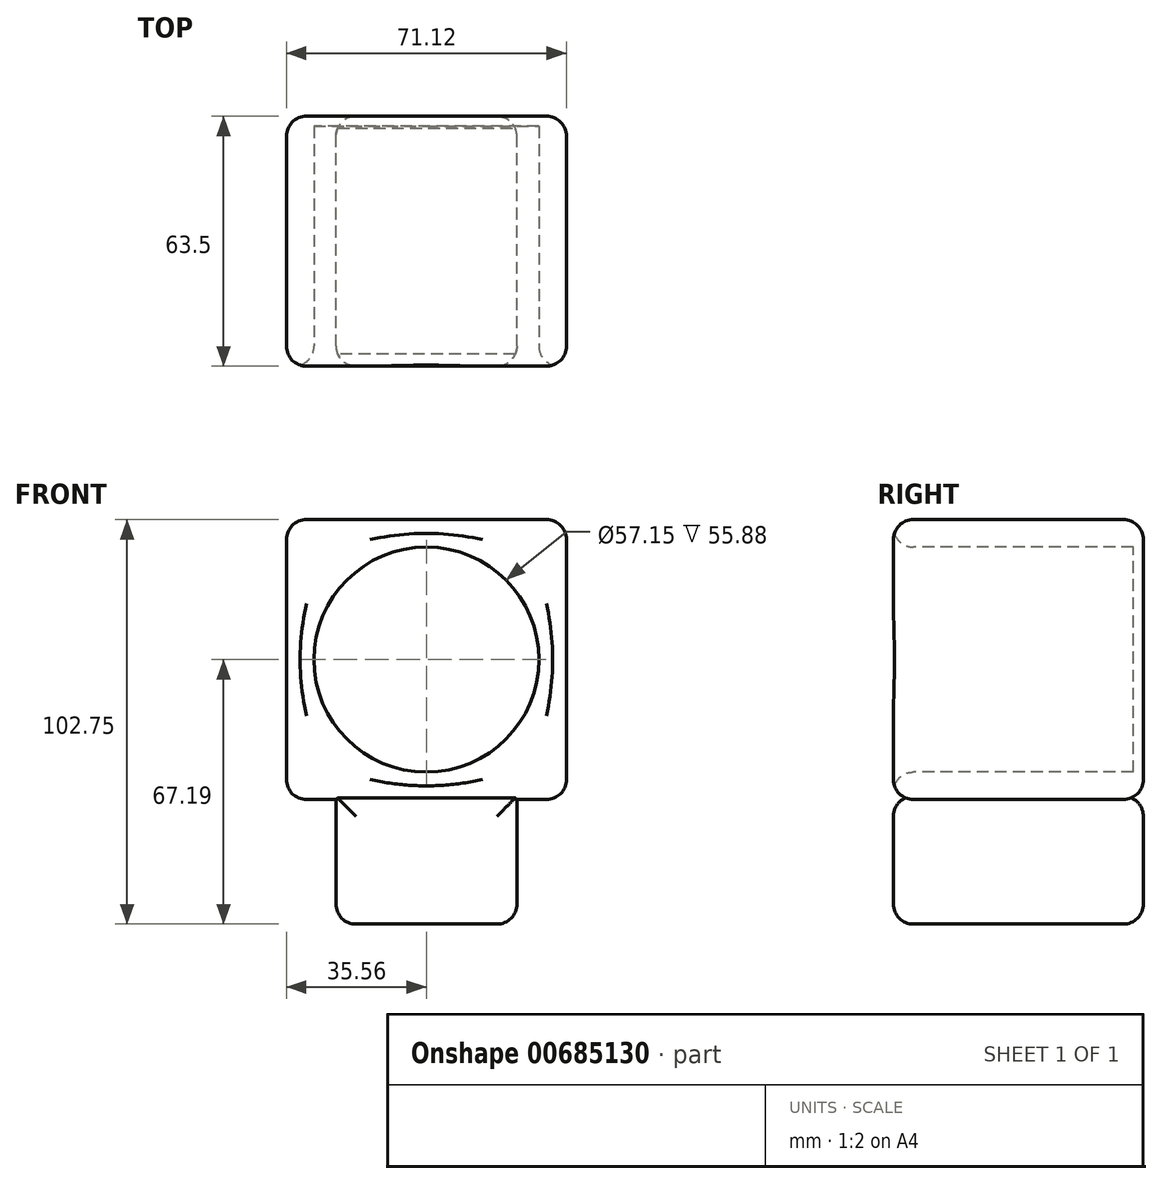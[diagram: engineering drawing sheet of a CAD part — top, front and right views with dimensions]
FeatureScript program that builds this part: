
annotation { "Feature Type Name" : "Feature", "Feature Type Description" : "" }
export const myFeature = defineFeature(function(context is Context, id is Id, definition is map)
    precondition{}
    {
        {
            var Q0;
            Q0=qCreatedBy(makeId("Front.planeOp"),FACE);
            var sketch = newSketch(context, id + "F0", { "sketchPlane" : qUnion([Q0])});
            skLineSegment(sketch, "E0.bottom", {"start": v(-35.56, 35.56) * mm, "end": v(35.56, 35.56) * mm});
            skLineSegment(sketch, "E0.top", {"start": v(-35.56, -35.56) * mm, "end": v(35.56, -35.56) * mm});
            skLineSegment(sketch, "E0.left", {"start": v(-35.56, 35.56) * mm, "end": v(-35.56, -35.56) * mm});
            skLineSegment(sketch, "E0.right", {"start": v(35.56, 35.56) * mm, "end": v(35.56, -35.56) * mm});
            skPoint(sketch, "E0.middle", {"position": v(0, 0) * mm});
            skSolve(sketch);
        }
        {
            var Q0;
            Q0=makeQuery(id+"F0.imprint","IMPRINT",FACE,{"disambiguationData":[TD([[makeQuery(id+"F0.imprint","IMPRINT",EDGE,{"derivedFrom":sQuery(id+"F0.wireOp",EDGE,"E0.bottom")}),-1.0]])]});
            extrude(context, id + "F1", {"entities" : qUnion([Q0]), "depth" : 63.5 * mm, "offsetDistance" : 25.4 * mm});
        }
        {
            var Q0;
            Q0=makeQuery(id+"F1.opExtrude","CAP_FACE",FACE,{"disambiguationData":[OSD([sQuery(id+"F0.wireOp",EDGE,"E0.bottom"),sQuery(id+"F0.wireOp",EDGE,"E0.top"),sQuery(id+"F0.wireOp",EDGE,"E0.left"),sQuery(id+"F0.wireOp",EDGE,"E0.right")])],"isStart":false});
            var sketch = newSketch(context, id + "F2", { "sketchPlane" : qUnion([Q0])});
            skCircle(sketch, "E1", {"center": v(0, 0) * mm, "radius": 28.58 * mm});
            skSolve(sketch);
        }
        {
            var Q0;
            Q0=qCreatedBy(makeId("Front.planeOp"),FACE);
            var sketch = newSketch(context, id + "F3", { "sketchPlane" : qUnion([Q0])});
            skLineSegment(sketch, "E2.bottom", {"start": v(22.99, -35.14) * mm, "end": v(-22.99, -35.14) * mm});
            skLineSegment(sketch, "E2.top", {"start": v(22.99, -67.2) * mm, "end": v(-22.99, -67.2) * mm});
            skLineSegment(sketch, "E2.left", {"start": v(22.99, -35.14) * mm, "end": v(22.99, -67.2) * mm});
            skLineSegment(sketch, "E2.right", {"start": v(-22.99, -35.14) * mm, "end": v(-22.99, -67.2) * mm});
            skPoint(sketch, "E2.middle", {"position": v(0, -51.17) * mm});
            skSolve(sketch);
        }
        {
            var Q0;
            Q0=makeQuery(id+"F2.imprint","IMPRINT",FACE,{"disambiguationData":[TD([[makeQuery(id+"F2.imprint","IMPRINT",EDGE,{"derivedFrom":sQuery(id+"F2.wireOp",EDGE,"E1")}),1.0]])]});
            extrude(context, id + "F4", {"entities" : qUnion([Q0]), "operationType" : NewBodyOperationType.REMOVE, "oppositeDirection" : true, "depth" : 60.96 * mm, "offsetDistance" : 25.4 * mm});
        }
        {
            var Q0;
            Q0=makeQuery(id+"F1.opExtrude","CAP_FACE",FACE,{"disambiguationData":[OSD([sQuery(id+"F0.wireOp",EDGE,"E0.bottom"),sQuery(id+"F0.wireOp",EDGE,"E0.top"),sQuery(id+"F0.wireOp",EDGE,"E0.left"),sQuery(id+"F0.wireOp",EDGE,"E0.right")])],"isStart":false});
            fillet(context, id + "F5", {"entities" : qUnion([Q0]), "radius" : 5.08 * mm, "tangentPropagation" : true, "allowEdgeOverflow" : false});
        }
        {
            var Q0;
            Q0=makeQuery(id+"F1.opExtrude","CAP_FACE",FACE,{"disambiguationData":[OSD([sQuery(id+"F0.wireOp",EDGE,"E0.bottom"),sQuery(id+"F0.wireOp",EDGE,"E0.top"),sQuery(id+"F0.wireOp",EDGE,"E0.left"),sQuery(id+"F0.wireOp",EDGE,"E0.right")])],"isStart":true});
            fillet(context, id + "F6", {"entities" : qUnion([Q0]), "radius" : 5.08 * mm, "tangentPropagation" : true, "allowEdgeOverflow" : false});
        }
        {
            var Q0;
            Q0=makeQuery(id+"F1.opExtrude","SWEPT_FACE",FACE,{"disambiguationData":[OSD([sQuery(id+"F0.wireOp",EDGE,"E0.bottom")])]});
            fillet(context, id + "F7", {"entities" : qUnion([Q0]), "radius" : 5.08 * mm, "tangentPropagation" : true, "allowEdgeOverflow" : false});
        }
        {
            var Q0;
            Q0=makeQuery(id+"F1.opExtrude","SWEPT_FACE",FACE,{"disambiguationData":[OSD([sQuery(id+"F0.wireOp",EDGE,"E0.right")])]});
            fillet(context, id + "F8", {"entities" : qUnion([Q0]), "radius" : 5.08 * mm, "tangentPropagation" : true, "allowEdgeOverflow" : false});
        }
        {
            var Q0;
            Q0=makeQuery(id+"F1.opExtrude","SWEPT_FACE",FACE,{"disambiguationData":[OSD([sQuery(id+"F0.wireOp",EDGE,"E0.left")])]});
            fillet(context, id + "F9", {"entities" : qUnion([Q0]), "radius" : 5.08 * mm, "tangentPropagation" : true, "allowEdgeOverflow" : false});
        }
        {
            var Q0;
            Q0=makeQuery(id+"F3.imprint","IMPRINT",FACE,{"disambiguationData":[TD([[makeQuery(id+"F3.imprint","IMPRINT",EDGE,{"derivedFrom":sQuery(id+"F3.wireOp",EDGE,"E2.bottom")}),1.0]])]});
            extrude(context, id + "F10", {"entities" : qUnion([Q0]), "operationType" : NewBodyOperationType.ADD, "depth" : 63.5 * mm, "offsetDistance" : 25.4 * mm});
        }
        {
            var Q0;
            Q0=makeQuery(id+"F10.opExtrude","CAP_FACE",FACE,{"disambiguationData":[OSD([sQuery(id+"F3.wireOp",EDGE,"E2.bottom"),sQuery(id+"F3.wireOp",EDGE,"E2.top"),sQuery(id+"F3.wireOp",EDGE,"E2.left"),sQuery(id+"F3.wireOp",EDGE,"E2.right")])],"isStart":false});
            fillet(context, id + "F11", {"entities" : qUnion([Q0]), "radius" : 5.08 * mm, "tangentPropagation" : true, "allowEdgeOverflow" : false});
        }
        {
            var Q0;
            Q0=makeQuery(id+"F10.opExtrude","SWEPT_FACE",FACE,{"disambiguationData":[OSD([sQuery(id+"F3.wireOp",EDGE,"E2.top")])]});
            fillet(context, id + "F12", {"entities" : qUnion([Q0]), "radius" : 5.08 * mm, "tangentPropagation" : true, "allowEdgeOverflow" : false});
        }
        {
            var Q0;
            Q0=makeQuery(id+"F10.opExtrude","CAP_FACE",FACE,{"disambiguationData":[OSD([sQuery(id+"F3.wireOp",EDGE,"E2.bottom"),sQuery(id+"F3.wireOp",EDGE,"E2.top"),sQuery(id+"F3.wireOp",EDGE,"E2.left"),sQuery(id+"F3.wireOp",EDGE,"E2.right")])],"isStart":true});
            fillet(context, id + "F13", {"entities" : qUnion([Q0]), "radius" : 5.08 * mm, "tangentPropagation" : true, "allowEdgeOverflow" : false});
        }
    });
